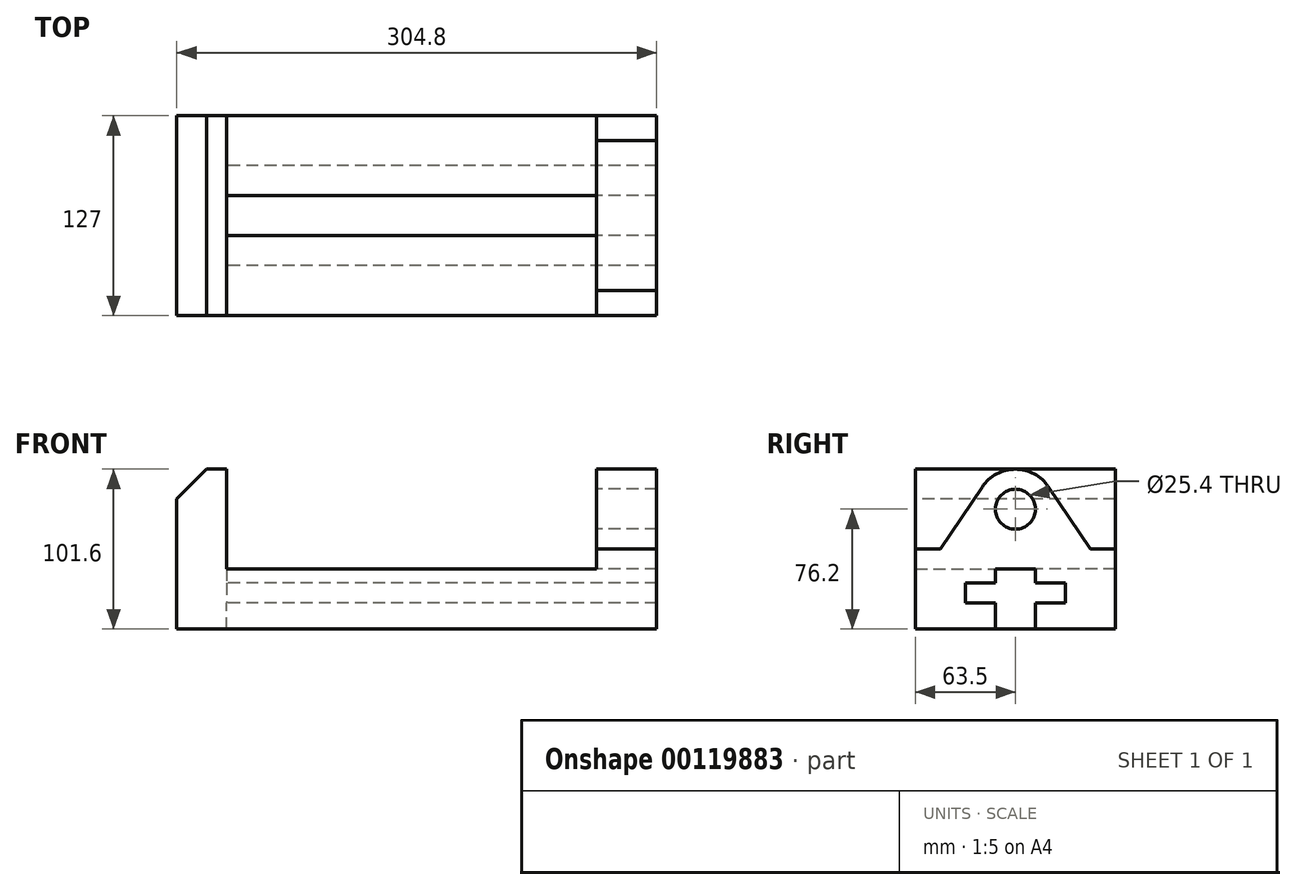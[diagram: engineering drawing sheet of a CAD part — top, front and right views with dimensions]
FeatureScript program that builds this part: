
annotation { "Feature Type Name" : "Feature", "Feature Type Description" : "" }
export const myFeature = defineFeature(function(context is Context, id is Id, definition is map)
    precondition{}
    {
        {
            var Q0;
            Q0=qCreatedBy(makeId("Right.planeOp"),FACE);
            var sketch = newSketch(context, id + "F0", { "sketchPlane" : qUnion([Q0])});
            skLineSegment(sketch, "E0", {"start": v(-12.7, 0) * mm, "end": v(-12.7, 16.51) * mm});
            skLineSegment(sketch, "E1", {"start": v(-12.7, 16.51) * mm, "end": v(-31.75, 16.51) * mm});
            skLineSegment(sketch, "E2", {"start": v(-31.75, 16.51) * mm, "end": v(-31.75, 29.21) * mm});
            skLineSegment(sketch, "E3", {"start": v(-31.75, 29.21) * mm, "end": v(-12.7, 29.21) * mm});
            skLineSegment(sketch, "E4", {"start": v(-12.7, 29.21) * mm, "end": v(-12.7, 38.1) * mm});
            skLineSegment(sketch, "E5", {"start": v(-12.7, 38.1) * mm, "end": v(12.7, 38.1) * mm});
            skLineSegment(sketch, "E6", {"start": v(12.7, 38.1) * mm, "end": v(12.7, 29.21) * mm});
            skLineSegment(sketch, "E7", {"start": v(12.7, 29.21) * mm, "end": v(31.75, 29.21) * mm});
            skLineSegment(sketch, "E8", {"start": v(31.75, 29.21) * mm, "end": v(31.75, 16.51) * mm});
            skLineSegment(sketch, "E9", {"start": v(31.75, 16.51) * mm, "end": v(12.7, 16.51) * mm});
            skLineSegment(sketch, "E10", {"start": v(12.7, 16.51) * mm, "end": v(12.7, 0) * mm});
            skArc(sketch, "E11", {"start": v(-21.1, 90.35) * mm, "mid": v(0, 101.6) * mm, "end": v(21.1, 90.35) * mm});
            skCircle(sketch, "E12", {"center": v(0, 76.2) * mm, "radius": 12.7 * mm});
            skLineSegment(sketch, "E13", {"start": v(-63.5, 50.8) * mm, "end": v(-63.5, 0) * mm});
            skLineSegment(sketch, "E14", {"start": v(63.5, 0) * mm, "end": v(63.5, 50.8) * mm});
            skLineSegment(sketch, "E15", {"start": v(47.62, 50.8) * mm, "end": v(21.1, 90.35) * mm});
            skLineSegment(sketch, "E16", {"start": v(-47.62, 50.8) * mm, "end": v(-21.1, 90.35) * mm});
            skLineSegment(sketch, "E17", {"start": v(-12.7, 0) * mm, "end": v(-63.5, 0) * mm});
            skLineSegment(sketch, "E18", {"start": v(12.7, 0) * mm, "end": v(63.5, 0) * mm});
            skLineSegment(sketch, "E19", {"start": v(63.5, 50.8) * mm, "end": v(47.62, 50.8) * mm});
            skLineSegment(sketch, "E20", {"start": v(-63.5, 50.8) * mm, "end": v(-47.62, 50.8) * mm});
            skSolve(sketch);
        }
        {
            var Q0;
            Q0 = qSketchRegion(id + "F0", true);
            extrude(context, id + "F1", {"entities" : qUnion([Q0]), "depth" : 38.1 * mm});
        }
        {
            var Q0;
            Q0=qCreatedBy(makeId("Right.planeOp"),FACE);
            var sketch = newSketch(context, id + "F2", { "sketchPlane" : qUnion([Q0])});
            skLineSegment(sketch, "E21", {"start": v(12.7, 0) * mm, "end": v(12.7, 16.51) * mm});
            skLineSegment(sketch, "E22", {"start": v(12.7, 16.51) * mm, "end": v(31.75, 16.51) * mm});
            skLineSegment(sketch, "E23", {"start": v(31.75, 16.51) * mm, "end": v(31.75, 29.21) * mm});
            skLineSegment(sketch, "E24", {"start": v(31.75, 29.21) * mm, "end": v(12.7, 29.21) * mm});
            skLineSegment(sketch, "E25", {"start": v(12.7, 29.21) * mm, "end": v(12.7, 38.1) * mm});
            skLineSegment(sketch, "E26", {"start": v(12.7, 38.1) * mm, "end": v(-12.7, 38.1) * mm, "construction": true});
            skLineSegment(sketch, "E27", {"start": v(-12.7, 38.1) * mm, "end": v(-12.7, 29.21) * mm});
            skLineSegment(sketch, "E28", {"start": v(-12.7, 29.2) * mm, "end": v(-31.75, 29.2) * mm});
            skLineSegment(sketch, "E29", {"start": v(-31.75, 29.21) * mm, "end": v(-31.75, 16.51) * mm});
            skLineSegment(sketch, "E30", {"start": v(-31.75, 16.51) * mm, "end": v(-12.7, 16.51) * mm});
            skLineSegment(sketch, "E31", {"start": v(-12.7, 16.51) * mm, "end": v(-12.7, 0) * mm});
            skLineSegment(sketch, "E32", {"start": v(-12.7, 0) * mm, "end": v(-63.5, 0) * mm});
            skLineSegment(sketch, "E33", {"start": v(-63.5, 0) * mm, "end": v(-63.5, 38.1) * mm});
            skLineSegment(sketch, "E34", {"start": v(-63.5, 38.1) * mm, "end": v(-12.7, 38.1) * mm});
            skLineSegment(sketch, "E35", {"start": v(12.7, 0) * mm, "end": v(63.5, 0) * mm});
            skLineSegment(sketch, "E36", {"start": v(63.5, 0) * mm, "end": v(63.5, 38.1) * mm});
            skLineSegment(sketch, "E37", {"start": v(63.5, 38.1) * mm, "end": v(12.7, 38.1) * mm});
            skSolve(sketch);
        }
        {
            var Q0;
            Q0 = qSketchRegion(id + "F2", true);
            extrude(context, id + "F3", {"entities" : qUnion([Q0]), "operationType" : NewBodyOperationType.ADD, "oppositeDirection" : true, "depth" : 266.7 * mm});
        }
        {
            var Q0;
            Q0=makeQuery(id+"F3.boolean.opBoolean","MERGE",FACE,{"derivedFrom":[makeQuery(id+"F1.opExtrude","SWEPT_FACE",FACE,{"disambiguationData":[OSD([sQuery(id+"F0.wireOp",EDGE,"KOMfF8rO-Nzvu-hCZF-JWwZ-14JNZTLsuZos")])]}),makeQuery(id+"F3.opExtrude","SWEPT_FACE",FACE,{"disambiguationData":[OSD([sQuery(id+"F2.wireOp",EDGE,"E33")])]})]});
            var sketch = newSketch(context, id + "F4", { "sketchPlane" : qUnion([Q0])});
            skLineSegment(sketch, "E38", {"start": v(-266.7, 0) * mm, "end": v(-266.7, 82.55) * mm});
            skLineSegment(sketch, "E39", {"start": v(-266.7, 82.55) * mm, "end": v(-247.65, 101.6) * mm});
            skLineSegment(sketch, "E40", {"start": v(-247.65, 101.6) * mm, "end": v(-234.95, 101.6) * mm});
            skLineSegment(sketch, "E41", {"start": v(-234.95, 101.6) * mm, "end": v(-234.95, 0) * mm});
            skLineSegment(sketch, "E42", {"start": v(-234.95, 0) * mm, "end": v(-266.7, 0) * mm});
            skLineSegment(sketch, "E43", {"start": v(-247.65, 101.6) * mm, "end": v(-266.7, 101.6) * mm, "construction": true});
            skLineSegment(sketch, "E44", {"start": v(-266.7, 101.6) * mm, "end": v(-266.7, 82.55) * mm, "construction": true});
            skSolve(sketch);
        }
        {
            var Q0;
            {var subQ6=sQuery(id+"F4.wireOp",EDGE,"E39");Q0=makeQuery(id+"F4.imprint","IMPRINT",FACE,{"disambiguationData":[TD([[makeQuery(id+"F4.imprint","IMPRINT",EDGE,{"derivedFrom":subQ6}),-1.0]])]});}
            var Q1;
            {var subQ0=sQuery(id+"F4.wireOp",EDGE,"E42");Q1=makeQuery(id+"F4.imprint","IMPRINT",FACE,{"disambiguationData":[TD([[makeQuery(id+"F4.imprint","IMPRINT",EDGE,{"derivedFrom":subQ0}),-1.0]])]});}
            var Q2;
            Q2 = qConstructionFilter(qBodyType(qCreatedBy(id + "F4" ,EDGE), BodyType.WIRE), ConstructionObject.NO);
            extrude(context, id + "F5", {"entities" : qUnion([Q0, Q1]), "operationType" : NewBodyOperationType.ADD, "surfaceEntities" : qUnion([Q2]), "oppositeDirection" : true, "depth" : 127 * mm});
        }
    });
